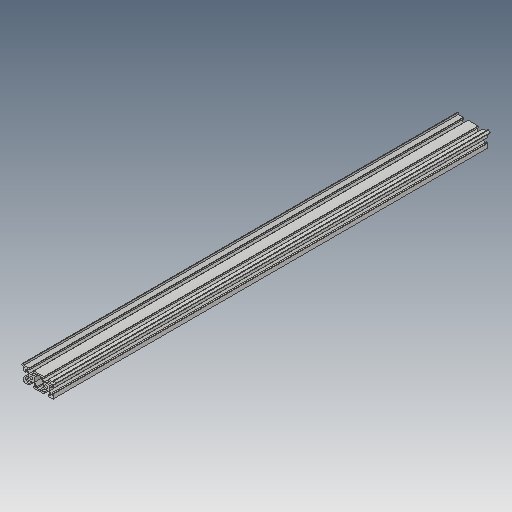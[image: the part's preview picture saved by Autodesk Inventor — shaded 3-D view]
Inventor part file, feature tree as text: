
AUTODESK INVENTOR PART (.ipt)
format: ipt  version: 2017 (Build 210142000, 142)  size: 234,496 bytes
history: native  units: mm
features: other x2, extrude x1, sketch x1, reference x1
ambient origin geometry x8: Origin, YZ Plane, XZ Plane, XY Plane, X Axis, Y Axis, Z Axis, Center Point
bodies: Solid1 (feature_tree)
feature tree (5):
  extrude  "Extrusion1"  [1 undecoded]
  sketch  "Sketch1"  dims[d0=585.0mm d1=0.0mm]
  reference  "Reference1"
  other  "Assembly3"
  other  "Makerslide 600mm:1"
note: 1 required parameter value undecoded (feature->parameter linkage not recoverable at this tier; creation-order binding heuristic only, values carry confidence <= 0.55)
